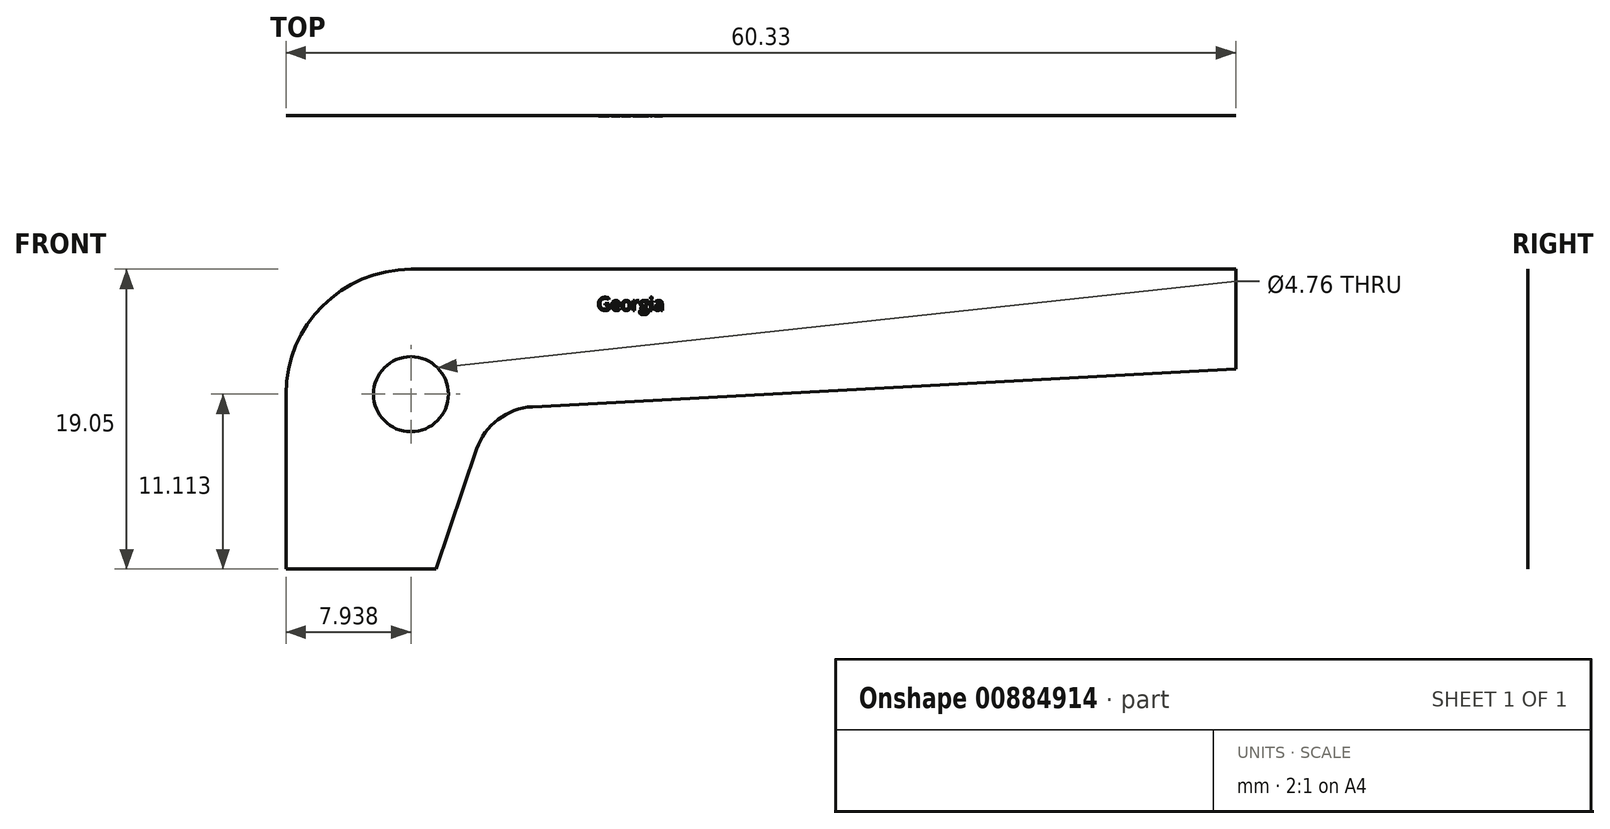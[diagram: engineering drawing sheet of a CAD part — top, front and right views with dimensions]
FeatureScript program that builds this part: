
annotation { "Feature Type Name" : "Feature", "Feature Type Description" : "" }
export const myFeature = defineFeature(function(context is Context, id is Id, definition is map)
    precondition{}
    {
        {
            var Q0;
            Q0=qCreatedBy(makeId("Front.planeOp"),FACE);
            var sketch = newSketch(context, id + "F0", { "sketchPlane" : qUnion([Q0])});
            skLineSegment(sketch, "E0.top", {"start": v(7.94, 19.05) * mm, "end": v(60.33, 19.05) * mm});
            skLineSegment(sketch, "E0.left", {"start": v(0, 0) * mm, "end": v(0, 11.11) * mm});
            skLineSegment(sketch, "E1", {"start": v(9.53, 0) * mm, "end": v(12.12, 7.63) * mm});
            skLineSegment(sketch, "E2", {"start": v(60.33, 12.7) * mm, "end": v(15.66, 10.31) * mm});
            skLineSegment(sketch, "E3", {"start": v(0, 0) * mm, "end": v(9.53, 0) * mm});
            skLineSegment(sketch, "E4", {"start": v(60.32, 19.05) * mm, "end": v(60.33, 12.7) * mm});
            skArc(sketch, "E5", {"start": v(15.66, 10.31) * mm, "mid": v(13.48, 9.51) * mm, "end": v(12.12, 7.63) * mm});
            skPoint(sketch, "E6.visualSharp", {"position": v(0, 19.05) * mm});
            skArc(sketch, "E6.filletArc", {"start": v(7.94, 19.05) * mm, "mid": v(2.32, 16.73) * mm, "end": v(0, 11.11) * mm});
            skSolve(sketch);
        }
        {
            var Q0;
            Q0 = qSketchRegion(id + "F0", true);
            extrude(context, id + "F1", {"entities" : qUnion([Q0]), "depth" : 3 / 812.8 * mm, "offsetDistance" : 25.4 * mm});
        }
        {
            var Q0;
            Q0=makeQuery(id+"F1.opExtrude","CAP_FACE",FACE,{"disambiguationData":[OSD([sQuery(id+"F0.wireOp",EDGE,"E0.top"),sQuery(id+"F0.wireOp",EDGE,"E0.left"),sQuery(id+"F0.wireOp",EDGE,"E1"),sQuery(id+"F0.wireOp",EDGE,"E2"),sQuery(id+"F0.wireOp",EDGE,"E3"),sQuery(id+"F0.wireOp",EDGE,"E4"),sQuery(id+"F0.wireOp",EDGE,"E5"),sQuery(id+"F0.wireOp",EDGE,"E6.filletArc")])],"isStart":false});
            var sketch = newSketch(context, id + "F2", { "sketchPlane" : qUnion([Q0])});
            skCircle(sketch, "E7", {"center": v(7.94, 11.11) * mm, "radius": 2.38 * mm});
            skSolve(sketch);
        }
        {
            var Q0;
            Q0=makeQuery(id+"F2.imprint","IMPRINT",FACE,{"disambiguationData":[TD([[makeQuery(id+"F2.imprint","IMPRINT",EDGE,{"derivedFrom":sQuery(id+"F2.wireOp",EDGE,"E7")}),1.0]])]});
            extrude(context, id + "F3", {"entities" : qUnion([Q0]), "operationType" : NewBodyOperationType.REMOVE, "oppositeDirection" : true, "depth" : 25.4 * mm, "offsetDistance" : 25.4 * mm});
        }
        {
            var Q0;
            Q0=makeQuery(id+"F1.opExtrude","SWEPT_FACE",FACE,{"disambiguationData":[OSD([sQuery(id+"F0.wireOp",EDGE,"E0.top")])]});
            var sketch = newSketch(context, id + "F4", { "sketchPlane" : qUnion([Q0])});
            skLineSegment(sketch, "E8", {"start": v(45.24, 0) * mm, "end": v(60.33, -0.8) * mm});
            skLineSegment(sketch, "E9", {"start": v(60.33, -0.8) * mm, "end": v(60.33, 0) * mm});
            skLineSegment(sketch, "E10", {"start": v(60.33, 0) * mm, "end": v(45.24, 0) * mm});
            skLineSegment(sketch, "E11.MirrorCS", {"start": v(60.33, -2.38) * mm, "end": v(45.24, -2.38) * mm});
            skLineSegment(sketch, "E12.MirrorCS", {"start": v(45.24, -2.38) * mm, "end": v(60.33, -1.59) * mm});
            skLineSegment(sketch, "E13.MirrorCS", {"start": v(60.33, -1.59) * mm, "end": v(60.33, -2.38) * mm});
            skSolve(sketch);
        }
        {
            var Q0;
            Q0=makeQuery(id+"F4.imprint","IMPRINT",FACE,{"disambiguationData":[TD([[makeQuery(id+"F4.imprint","IMPRINT",EDGE,{"derivedFrom":sQuery(id+"F4.wireOp",EDGE,"E11.MirrorCS")}),1.0]])]});
            var Q1;
            Q1=makeQuery(id+"F4.imprint","IMPRINT",FACE,{"disambiguationData":[TD([[makeQuery(id+"F4.imprint","IMPRINT",EDGE,{"derivedFrom":sQuery(id+"F4.wireOp",EDGE,"E8")}),1.0]])]});
            extrude(context, id + "F5", {"entities" : qUnion([Q0, Q1]), "operationType" : NewBodyOperationType.REMOVE, "oppositeDirection" : true, "depth" : 25.4 * mm, "offsetDistance" : 25.4 * mm});
        }
        {
            var Q0;
            Q0=makeQuery(id+"F1.opExtrude","CAP_FACE",FACE,{"disambiguationData":[OSD([sQuery(id+"F0.wireOp",EDGE,"E0.top"),sQuery(id+"F0.wireOp",EDGE,"E0.left"),sQuery(id+"F0.wireOp",EDGE,"E1"),sQuery(id+"F0.wireOp",EDGE,"E2"),sQuery(id+"F0.wireOp",EDGE,"E3"),sQuery(id+"F0.wireOp",EDGE,"E4"),sQuery(id+"F0.wireOp",EDGE,"E5"),sQuery(id+"F0.wireOp",EDGE,"E6.filletArc")])],"isStart":false});
            var sketch = newSketch(context, id + "F6", { "sketchPlane" : qUnion([Q0])});
            skText(sketch, "E14", { "text": "Georgia", "fontName": "OpenSans-Regular.ttf"});
            const initialGuessF6  = {"E14": [0.01978, 0.01644, 1, 0, 0.00083]};
            skSetInitialGuess(sketch, initialGuessF6);
            skSolve(sketch);
        }
        {
            var Q0;
            Q0 = qSketchRegion(id + "F6", true);
            extrude(context, id + "F7", {"entities" : qUnion([Q0]), "operationType" : NewBodyOperationType.ADD, "depth" : 1 / 1625.6 * mm, "offsetDistance" : 25.4 * mm});
        }
    });
